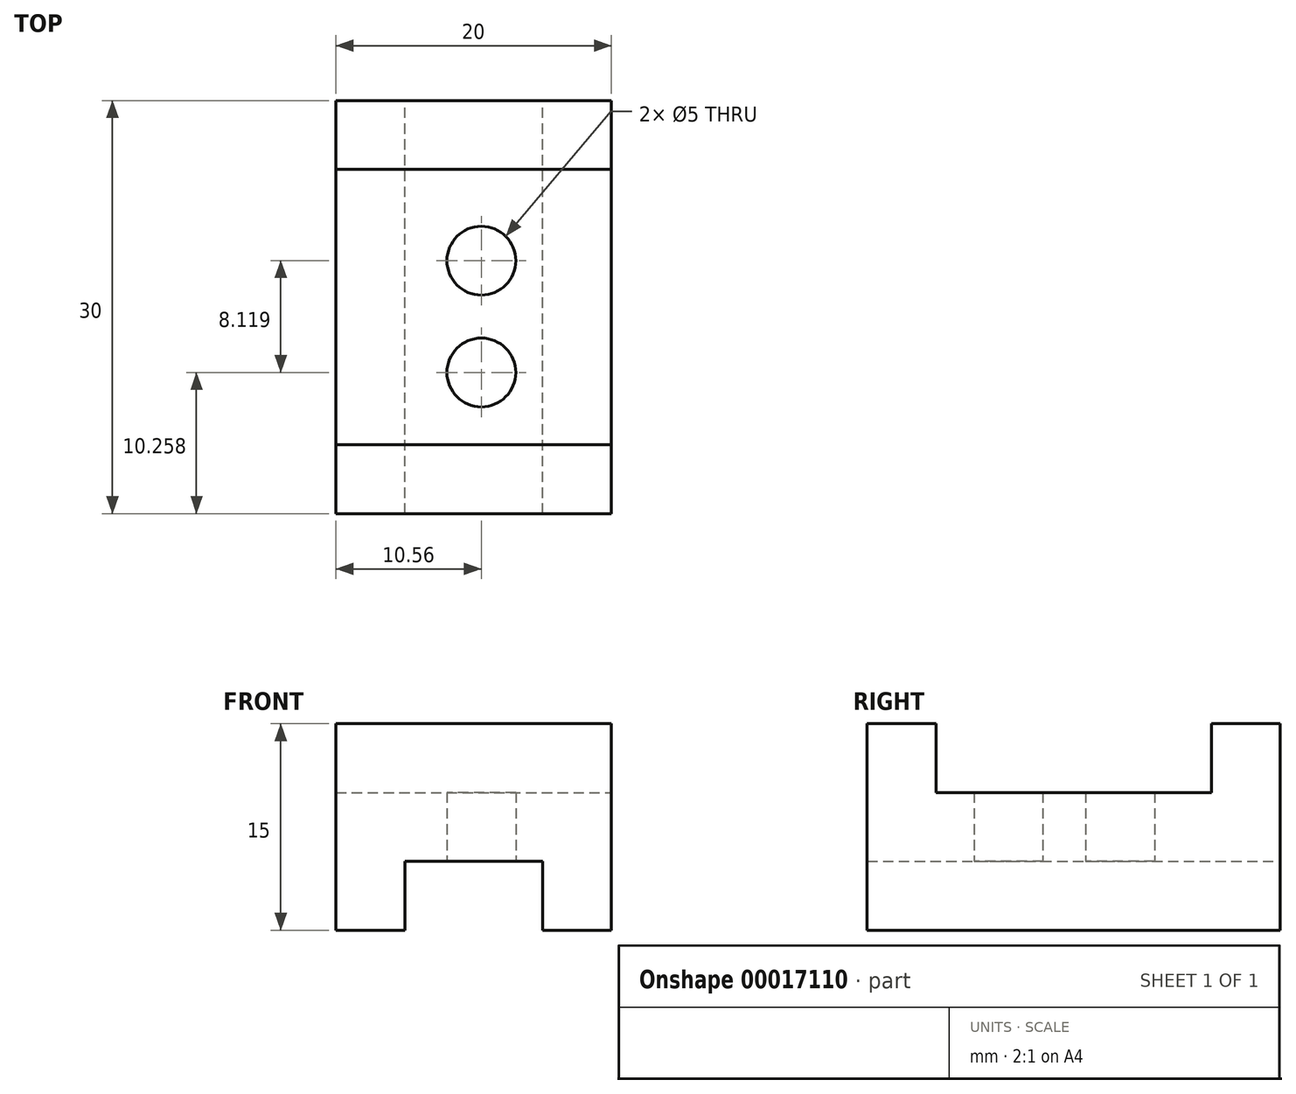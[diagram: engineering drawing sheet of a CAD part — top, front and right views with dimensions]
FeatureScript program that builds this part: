
annotation { "Feature Type Name" : "Feature", "Feature Type Description" : "" }
export const myFeature = defineFeature(function(context is Context, id is Id, definition is map)
    precondition{}
    {
        {
            var Q0;
            Q0=qCreatedBy(makeId("Front.planeOp"),FACE);
            var sketch = newSketch(context, id + "F0", { "sketchPlane" : qUnion([Q0])});
            skLineSegment(sketch, "E0", {"start": v(-10.56, 23.41) * mm, "end": v(9.44, 23.41) * mm});
            skLineSegment(sketch, "E1", {"start": v(9.44, 23.41) * mm, "end": v(9.44, 8.41) * mm});
            skLineSegment(sketch, "E2", {"start": v(9.44, 8.41) * mm, "end": v(4.44, 8.41) * mm});
            skLineSegment(sketch, "E3", {"start": v(4.44, 8.41) * mm, "end": v(4.44, 13.41) * mm});
            skLineSegment(sketch, "E4", {"start": v(4.44, 13.41) * mm, "end": v(-5.56, 13.41) * mm});
            skLineSegment(sketch, "E5", {"start": v(-5.56, 13.41) * mm, "end": v(-5.56, 8.41) * mm});
            skLineSegment(sketch, "E6", {"start": v(-5.56, 8.41) * mm, "end": v(-10.56, 8.41) * mm});
            skLineSegment(sketch, "E7", {"start": v(-10.56, 8.41) * mm, "end": v(-10.56, 23.41) * mm});
            skSolve(sketch);
        }
        {
            var Q0;
            Q0 = qSketchRegion(id + "F0", true);
            var Q1;
            Q1=makeQuery(id+"F0.imprint","IMPRINT",FACE,{"disambiguationData":[TD([[makeQuery(id+"F0.imprint","IMPRINT",EDGE,{"derivedFrom":sQuery(id+"F0.wireOp",EDGE,"E0")}),-1.0]])]});
            extrude(context, id + "F1", {"entities" : qUnion([Q0, Q1]), "depth" : 30 * mm});
        }
        {
            var Q0;
            Q0=makeQuery(id+"F1.opExtrude","SWEPT_FACE",FACE,{"disambiguationData":[OSD([sQuery(id+"F0.wireOp",EDGE,"E0")])]});
            var sketch = newSketch(context, id + "F2", { "sketchPlane" : qUnion([Q0])});
            skLineSegment(sketch, "E8", {"start": v(-10.56, -25) * mm, "end": v(9.44, -25) * mm});
            skLineSegment(sketch, "E9", {"start": v(-10.56, -5) * mm, "end": v(9.44, -5) * mm});
            skLineSegment(sketch, "E10", {"start": v(-10.56, -5) * mm, "end": v(-10.56, -25) * mm});
            skLineSegment(sketch, "E11", {"start": v(9.44, -5) * mm, "end": v(9.44, -25) * mm});
            skSolve(sketch);
        }
        {
            var Q0;
            Q0=makeQuery(id+"F2.imprint","IMPRINT",FACE,{"disambiguationData":[TD([[makeQuery(id+"F2.imprint","IMPRINT",EDGE,{"derivedFrom":sQuery(id+"F2.wireOp",EDGE,"E8")}),1.0]])]});
            extrude(context, id + "F3", {"entities" : qUnion([Q0]), "operationType" : NewBodyOperationType.REMOVE, "oppositeDirection" : true, "depth" : 5 * mm});
        }
        {
            var Q0;
            Q0=qCreatedBy(makeId("Top.planeOp"),FACE);
            var sketch = newSketch(context, id + "F4", { "sketchPlane" : qUnion([Q0])});
            skLineSegment(sketch, "E12", {"start": v(0, 0) * mm, "end": v(0, -28.32) * mm});
            skCircle(sketch, "E13", {"center": v(0, -11.62) * mm, "radius": 2.5 * mm});
            skCircle(sketch, "E14", {"center": v(0, -19.74) * mm, "radius": 2.5 * mm});
            skSolve(sketch);
        }
        {
            var Q0;
            Q0 = qSketchRegion(id + "F4", true);
            extrude(context, id + "F5", {"entities" : qUnion([Q0]), "operationType" : NewBodyOperationType.REMOVE, "depth" : 30 * mm});
        }
    });
